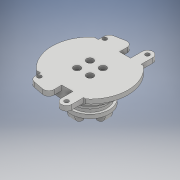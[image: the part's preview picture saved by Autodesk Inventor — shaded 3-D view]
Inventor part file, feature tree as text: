
AUTODESK INVENTOR PART (.ipt)
format: ipt  version: 2017 (Build 210142000, 142)  size: 515,072 bytes
history: native  units: mm
features: extrude x16, sketch x15, reference x6, other x4, chamfer x4, projected_geometry x3, plane x2, mirror x1, hole x1, boolean_combine x1, fillet x1
ambient origin geometry x8: Origin, YZ Plane, XZ Plane, XY Plane, X Axis, Y Axis, Z Axis, Center Point
bodies: Body1 (feature_tree), Body2 (feature_tree), Body3 (feature_tree)
feature tree (54):
  other  "Base Plate"
  extrude  "Extrusion1"  Depth=19.7mm
  extrude  "Extrusion2"  Depth=5.0mm
  chamfer  "Chamfer1"  Distance=8.0mm
  chamfer  "Chamfer2"  Distance=1.0mm Angle=45.0deg
  extrude  "Extrusion3"  Depth=5.0mm TaperAngle=0.0deg
  plane  "Work Plane1"
  mirror  "Mirror1"
  extrude  "Extrusion4"  Depth=1.75mm
  extrude  "Extrusion5"  Depth=6.9mm TaperAngle=0.0deg
  extrude  "Extrusion6"  Depth=4.3mm
  extrude  "Extrusion7"  Depth=40.0mm TaperAngle=360.0deg
  chamfer  "Chamfer4"  Distance=8.0mm
  extrude  "Extrusion8"  Depth=7.0mm
  extrude  "Extrusion9"  Depth=7.0mm
  extrude  "Extrusion10"  Depth=1.35mm TaperAngle=45.0deg
  extrude  "Extrusion11"  Depth=7.0mm TaperAngle=0.0deg
  sketch  "Sketch12"  dims[d50=3.9mm d51=0.0mm d52=35.0mm]
  extrude  "Extrusion12"  Depth=3.9mm
  extrude  "Extrusion13"  Depth=4.0mm TaperAngle=0.0deg
  extrude  "Extrusion14"  TaperAngle=45.0deg  [1 undecoded]
  extrude  "Extrusion15"  Depth=10.0mm TaperAngle=0.0deg
  extrude  "Extrusion16"  Depth=10.0mm TaperAngle=0.0deg
  hole  "Hole1"  [1 undecoded]
  boolean_combine  "Combine1"
  fillet  "Fillet1"  Radius=2.3mm
  chamfer  "Chamfer5"  Distance=40.0mm Angle=360.0deg
  sketch  "Sketch1"  dims[d0=22.0mm d1=19.7mm]
  reference  "Reference1"
  reference  "Reference2"
  reference  "Reference7"
  reference  "Reference8"
  sketch  "Sketch2"  dims[d2=5.0mm d3=0.0mm d6=53.0mm d7=8.0mm d8=0.0mm d9=1.0mm d10=2.0mm d11=45.0deg]
  projected_geometry  "Projected Loop1"
  reference  "Reference11"
  reference  "Reference12"
  sketch  "Sketch3"  dims[d12=10.0mm d13=8.5mm d14=45.0deg d18=5.0mm d19=0.0mm]
  plane  "Work Plane2"
  sketch  "Sketch4"  dims[d22=4.0mm d23=1.75mm d24=-7.853982mm]
  projected_geometry  "Projected Loop2"
  projected_geometry  "Projected Loop3"
  sketch  "Sketch5"  dims[d25=35.0mm d26=6.9mm d27=0.0mm]
  sketch  "Sketch6"  dims[d28=8.0mm d29=4.3mm]
  sketch  "Sketch7"  dims[d30=45.0deg d31=40.0mm d33=360.0deg d35=8.0mm d36=0.0mm]
  sketch  "Sketch8"  dims[d38=7.0mm d39=7.0mm]
  other  "Bearing Spacer"
  sketch  "Sketch9"  dims[d40=7.0mm d41=7.0mm]
  other  "Base Shaft"
  sketch  "Sketch10"  dims[d42=5.35mm d43=0.0mm d44=1.35mm d45=2.0mm d46=45.0deg]
  other  "Base Join"
  sketch  "Sketch11"  dims[d47=40.0mm d48=7.0mm d49=0.0mm]
  sketch  "Sketch13"  dims[d53=3.0mm d54=0.0mm d55=4.0mm d56=0.0mm]
  sketch  "Sketch14"  dims[d57=7.2mm d59=45.0deg]
  sketch  "Sketch15"  dims[d60=40.0mm d62=360.0deg d64=4.0mm d65=0.0mm d67=8.0mm d68=0.0mm d69=16.0mm d70=2.3mm d71=40.0mm d73=360.0deg d75=8.0mm d76=0.0mm d77=4.0mm d78=40.0mm d80=360.0deg d82=4.0mm d83=0.0mm d84=22.2mm d85=1.0mm d86=0.0mm d96=10.0mm d97=10.0mm d89=5.0mm d90=6.0mm d91=10.0mm d92=1.0mm d93=90.0deg d94=0.5mm d95=20.594885mm d98=8.0mm d99=1.0mm d100=2.0mm d101=45.0deg d102=39.5mm d103=39.5mm]
note: 2 required parameter values undecoded (feature->parameter linkage not recoverable at this tier; creation-order binding heuristic only, values carry confidence <= 0.55)
